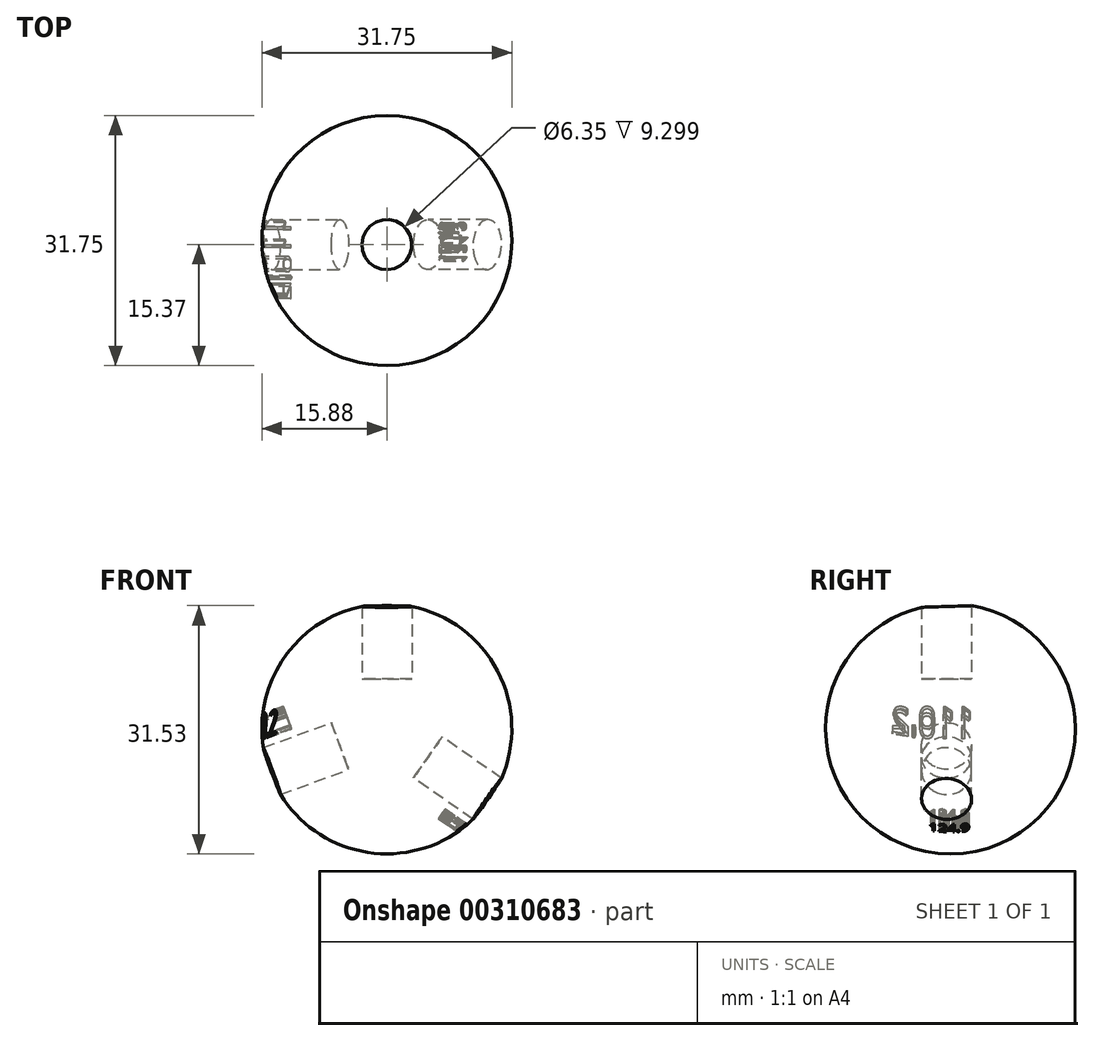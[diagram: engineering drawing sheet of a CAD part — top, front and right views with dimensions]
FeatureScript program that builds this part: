
annotation { "Feature Type Name" : "Feature", "Feature Type Description" : "" }
export const myFeature = defineFeature(function(context is Context, id is Id, definition is map)
    precondition{}
    {
        {
            var Q0;
            Q0=qCreatedBy(makeId("Top.planeOp"),FACE);
            var sketch = newSketch(context, id + "F0", { "sketchPlane" : qUnion([Q0])});
            skArc(sketch, "E0", {"start": v(0, 16.38) * mm, "mid": v(-15.88, 0.5) * mm, "end": v(0, -15.37) * mm});
            skLineSegment(sketch, "E1", {"start": v(0, 16.38) * mm, "end": v(0, -15.37) * mm});
            skSolve(sketch);
        }
        {
            var Q0;
            Q0=makeQuery(id+"F0.imprint","IMPRINT",FACE,{"disambiguationData":[TD([[makeQuery(id+"F0.imprint","IMPRINT",EDGE,{"derivedFrom":sQuery(id+"F0.wireOp",EDGE,"E0")}),1.0]])]});
            var Q1;
            Q1=sQuery(id+"F0.wireOp",EDGE,"E1");
            revolve(context, id + "F1", {"entities" : qUnion([Q0]), "axis" : qUnion([Q1]), "revolveType" : RevolveType.FULL});
        }
        {
            var Q0;
            Q0=qCreatedBy(makeId("Top.planeOp"),FACE);
            var sketch = newSketch(context, id + "F2", { "sketchPlane" : qUnion([Q0])});
            skLineSegment(sketch, "E2", {"start": v(0, 0) * mm, "end": v(56.78, 0) * mm, "construction": true});
            skLineSegment(sketch, "E3", {"start": v(0, 0) * mm, "end": v(0, 53.46) * mm, "construction": true});
            skSolve(sketch);
        }
        {
            var Q0;
            Q0=qCreatedBy(makeId("Top.planeOp"),FACE);
            cPlane(context, id + "F3", {"entities" : qUnion([Q0]), "cplaneType" : CPlaneType.OFFSET, "offset" : 6.35 * mm, "width" : 152.4 * mm, "height" : 152.4 * mm});
        }
        {
            var Q0;
            Q0=qCreatedBy(id+"F3.planeOp",FACE);
            var sketch = newSketch(context, id + "F4", { "sketchPlane" : qUnion([Q0])});
            skCircle(sketch, "E4", {"center": v(0, 0) * mm, "radius": 3.18 * mm});
            skSolve(sketch);
        }
        {
            var Q0;
            Q0 = qSketchRegion(id + "F4", true);
            extrude(context, id + "F5", {"entities" : qUnion([Q0]), "depth" : 38.1 * mm});
        }
        {
            var Q0;
            Q0=makeQuery(id+"F5.opExtrude","SWEPT_BODY",BODY,{"disambiguationData":[OSD([sQuery(id+"F4.wireOp",EDGE,"E4")])]});
            var Q1;
            Q1=sQuery(id+"F2.wireOp",EDGE,"E3");
            transform(context, id + "F6", {"entities" : qUnion([Q0]), "transformType" : TransformType.ROTATION, "transformAxis" : qUnion([Q1]), "angle" : 124.9 * degree, "makeCopy" : true});
        }
        {
            var Q0;
            Q0=makeQuery(id+"F6.opPattern","COPY",FACE,{"derivedFrom":makeQuery(id+"F5.opExtrude","CAP_FACE",FACE,{"disambiguationData":[OSD([sQuery(id+"F4.wireOp",EDGE,"E4")])],"isStart":false}),"instanceName":"1"});
            cPlane(context, id + "F7", {"entities" : qUnion([Q0]), "cplaneType" : CPlaneType.OFFSET, "offset" : 25.4 * mm, "oppositeDirection" : true, "width" : 152.4 * mm, "height" : 152.4 * mm});
        }
        {
            var Q0;
            Q0=makeQuery(id+"F6.opPattern","COPY",BODY,{"derivedFrom":makeQuery(id+"F5.opExtrude","SWEPT_BODY",BODY,{"disambiguationData":[OSD([sQuery(id+"F4.wireOp",EDGE,"E4")])]}),"instanceName":"1"});
            var Q1;
            Q1=sQuery(id+"F0.wireOp",EDGE,"E1");
            transform(context, id + "F8", {"entities" : qUnion([Q0]), "transformType" : TransformType.ROTATION, "transformAxis" : qUnion([Q1]), "angle" : 124.9 * degree, "oppositeDirection" : true, "makeCopy" : true});
        }
        {
            var Q0;
            Q0=qCreatedBy(id+"F7.planeOp",FACE);
            var sketch = newSketch(context, id + "F9", { "sketchPlane" : qUnion([Q0])});
            skText(sketch, "E5", { "text": "124.9\n", "fontName": "OpenSans-Regular.ttf"});
            const initialGuessF9  = {"E5": [-0.00225, -0.00557, 1, 0, 0.00146]};
            skSetInitialGuess(sketch, initialGuessF9);
            skSolve(sketch);
        }
        {
            var Q0;
            Q0 = qSketchRegion(id + "F9", true);
            extrude(context, id + "F10", {"entities" : qUnion([Q0]), "operationType" : NewBodyOperationType.REMOVE, "oppositeDirection" : true, "depth" : 7.11 * mm});
        }
        {
            var Q0;
            Q0=makeQuery(id+"F8.opPattern","COPY",FACE,{"derivedFrom":makeQuery(id+"F6.opPattern","COPY",FACE,{"derivedFrom":makeQuery(id+"F5.opExtrude","CAP_FACE",FACE,{"disambiguationData":[OSD([sQuery(id+"F4.wireOp",EDGE,"E4")])],"isStart":false}),"instanceName":"1"}),"instanceName":"1"});
            cPlane(context, id + "F11", {"entities" : qUnion([Q0]), "cplaneType" : CPlaneType.OFFSET, "offset" : 25.4 * mm, "oppositeDirection" : true, "width" : 152.4 * mm, "height" : 152.4 * mm});
        }
        {
            var Q0;
            Q0=qCreatedBy(id+"F11.planeOp",FACE);
            var sketch = newSketch(context, id + "F12", { "sketchPlane" : qUnion([Q0])});
            skText(sketch, "E6", { "text": "110.2", "fontName": "OpenSans-Regular.ttf"});
            const initialGuessF12  = {"E6": [-0.00336, 0.00425, 1, 0, 0.00294]};
            skSetInitialGuess(sketch, initialGuessF12);
            skSolve(sketch);
        }
        {
            var Q0;
            Q0 = qSketchRegion(id + "F12", true);
            extrude(context, id + "F13", {"entities" : qUnion([Q0]), "operationType" : NewBodyOperationType.REMOVE, "oppositeDirection" : true, "depth" : 7.67 * mm});
        }
        {
            var Q0;
            Q0=makeQuery(id+"F6.opPattern","COPY",BODY,{"derivedFrom":makeQuery(id+"F5.opExtrude","SWEPT_BODY",BODY,{"disambiguationData":[OSD([sQuery(id+"F4.wireOp",EDGE,"E4")])]}),"instanceName":"1"});
            var Q1;
            Q1=makeQuery(id+"F5.opExtrude","SWEPT_BODY",BODY,{"disambiguationData":[OSD([sQuery(id+"F4.wireOp",EDGE,"E4")])]});
            var Q2;
            Q2=makeQuery(id+"F8.opPattern","COPY",BODY,{"derivedFrom":makeQuery(id+"F6.opPattern","COPY",BODY,{"derivedFrom":makeQuery(id+"F5.opExtrude","SWEPT_BODY",BODY,{"disambiguationData":[OSD([sQuery(id+"F4.wireOp",EDGE,"E4")])]}),"instanceName":"1"}),"instanceName":"1"});
            var Q3;
            Q3=makeQuery(id+"F1.opRevolve","SWEPT_BODY",BODY,{"disambiguationData":[OSD([sQuery(id+"F0.wireOp",EDGE,"E0"),sQuery(id+"F0.wireOp",EDGE,"E1")])]});
            booleanBodies(context, id + "F14", {"operationType" : BooleanOperationType.SUBTRACTION, "tools" : qUnion([Q0, Q1, Q2]), "targets" : qUnion([Q3])});
        }
    });
